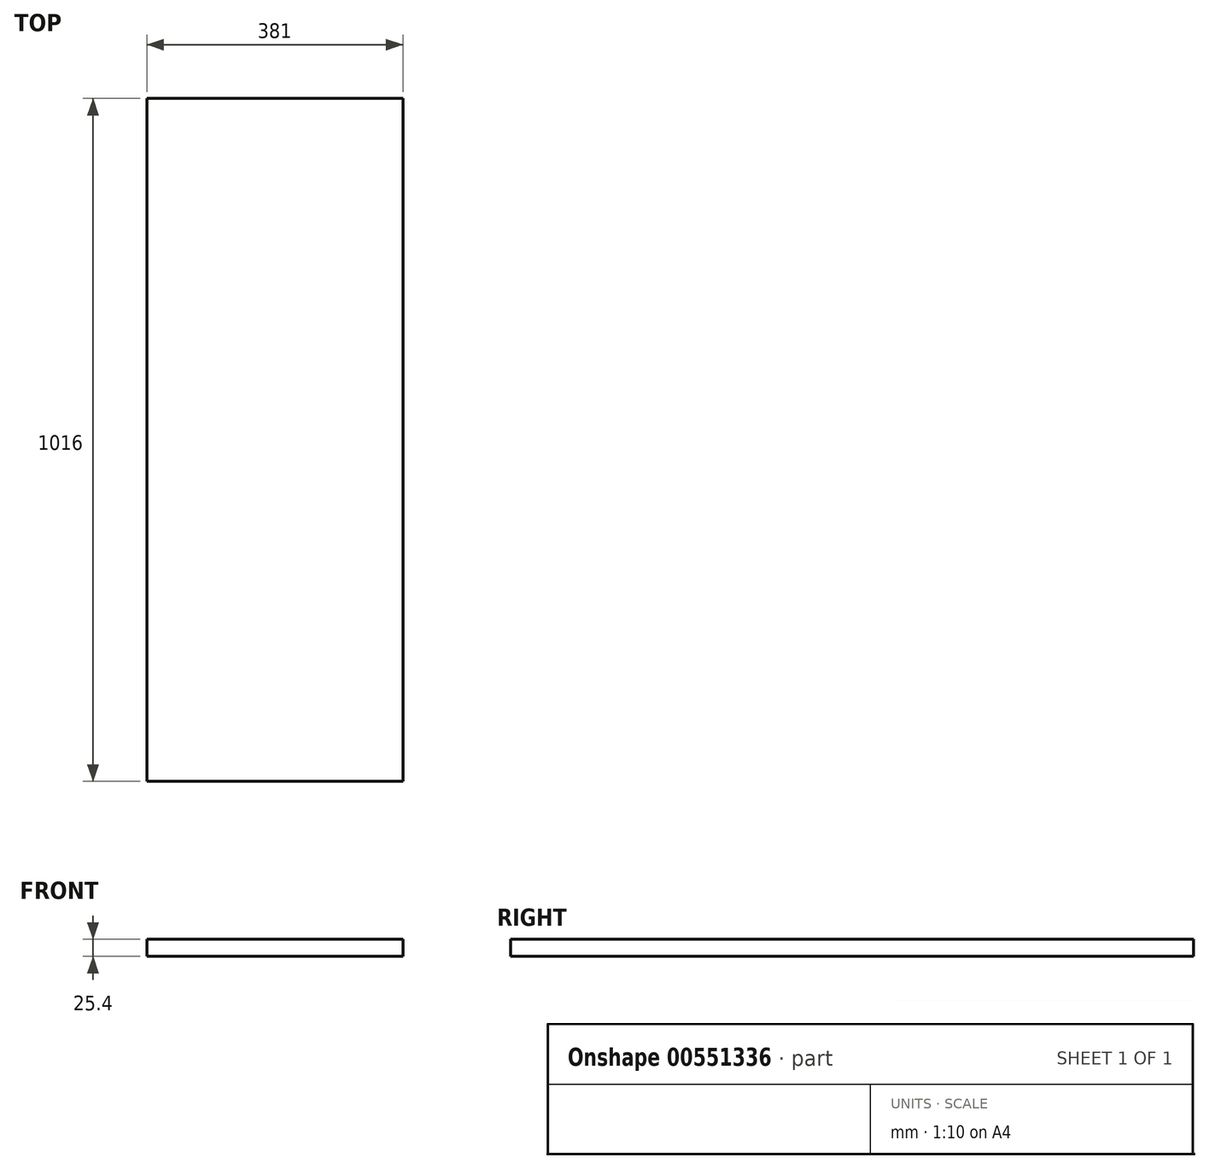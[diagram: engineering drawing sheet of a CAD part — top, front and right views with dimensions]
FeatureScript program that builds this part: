
annotation { "Feature Type Name" : "Feature", "Feature Type Description" : "" }
export const myFeature = defineFeature(function(context is Context, id is Id, definition is map)
    precondition{}
    {
        {
            var Q0;
            Q0=qCreatedBy(makeId("Top.planeOp"),FACE);
            var sketch = newSketch(context, id + "F0", { "sketchPlane" : qUnion([Q0])});
            skLineSegment(sketch, "E0.bottom", {"start": v(-203.74, 912.94) * mm, "end": v(177.26, 912.94) * mm});
            skLineSegment(sketch, "E0.top", {"start": v(-203.74, -103.06) * mm, "end": v(177.26, -103.06) * mm});
            skLineSegment(sketch, "E0.left", {"start": v(-203.74, 912.94) * mm, "end": v(-203.74, -103.06) * mm});
            skLineSegment(sketch, "E0.right", {"start": v(177.26, 912.94) * mm, "end": v(177.26, -103.06) * mm});
            skSolve(sketch);
        }
        {
            var Q0;
            Q0=makeQuery(id+"F0.imprint","IMPRINT",FACE,{"disambiguationData":[TD([[makeQuery(id+"F0.imprint","IMPRINT",EDGE,{"derivedFrom":sQuery(id+"F0.wireOp",EDGE,"E0.bottom")}),-1.0]])]});
            extrude(context, id + "F1", {"entities" : qUnion([Q0]), "depth" : 25.4 * mm, "offsetDistance" : 25.4 * mm});
        }
    });
